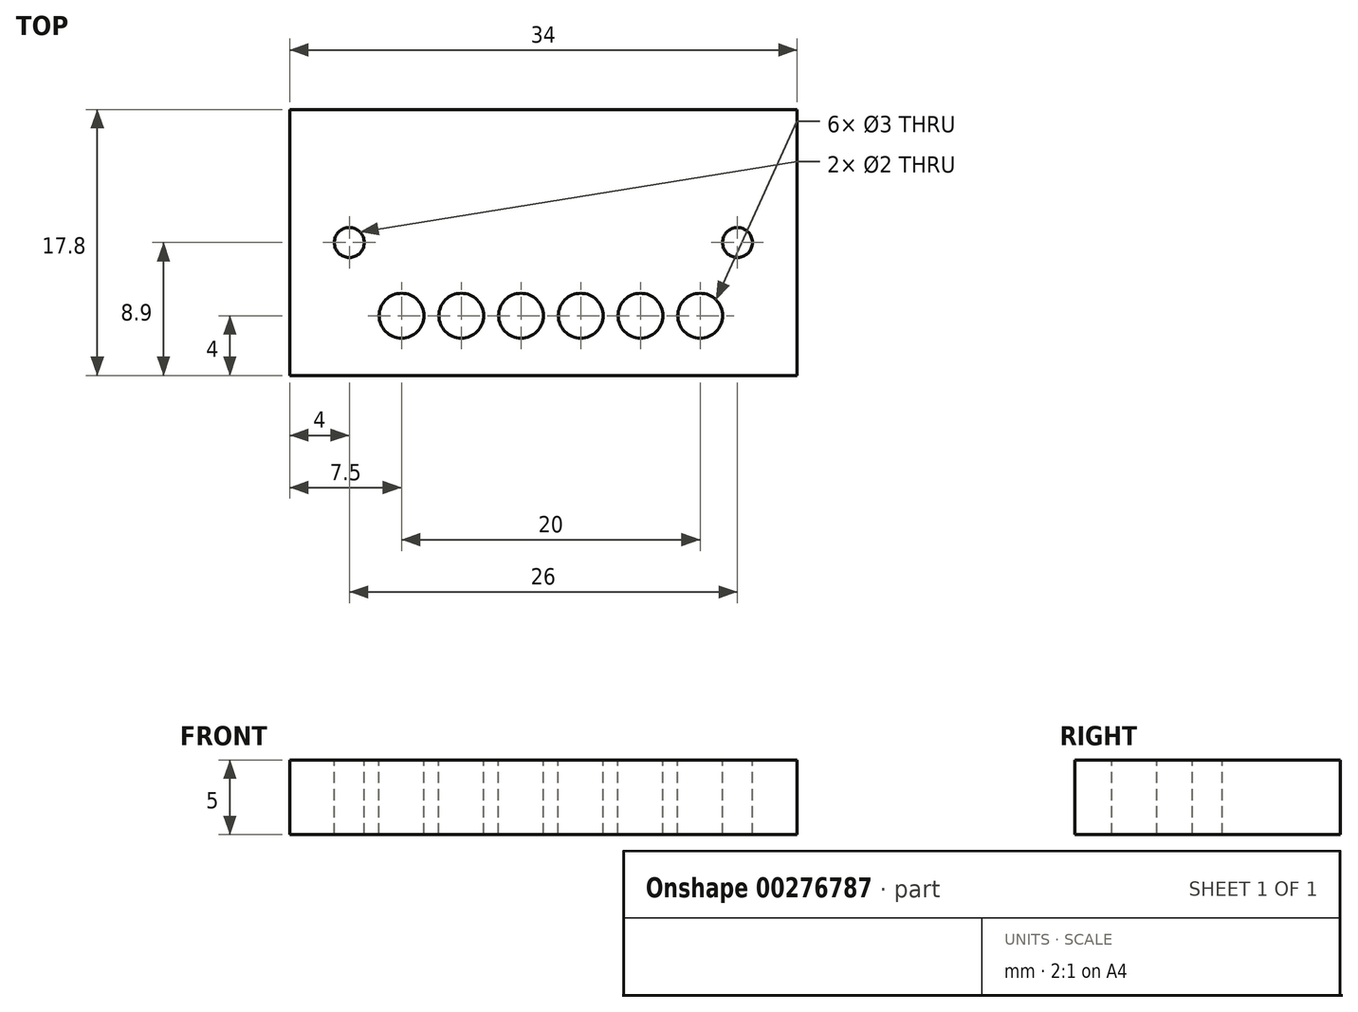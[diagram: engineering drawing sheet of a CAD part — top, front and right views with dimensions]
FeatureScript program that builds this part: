
annotation { "Feature Type Name" : "Feature", "Feature Type Description" : "" }
export const myFeature = defineFeature(function(context is Context, id is Id, definition is map)
    precondition{}
    {
        {
            var Q0;
            Q0=qCreatedBy(makeId("Top.planeOp"),FACE);
            var sketch = newSketch(context, id + "F0", { "sketchPlane" : qUnion([Q0])});
            skLineSegment(sketch, "E0.bottom", {"start": v(17, 8.9) * mm, "end": v(-17, 8.9) * mm});
            skLineSegment(sketch, "E0.top", {"start": v(17, -8.9) * mm, "end": v(-17, -8.9) * mm});
            skLineSegment(sketch, "E0.left", {"start": v(17, 8.9) * mm, "end": v(17, -8.9) * mm});
            skLineSegment(sketch, "E0.right", {"start": v(-17, 8.9) * mm, "end": v(-17, -8.9) * mm});
            skPoint(sketch, "E0.middle", {"position": v(0, 0) * mm});
            skSolve(sketch);
        }
        {
            var Q0;
            Q0=makeQuery(id+"F0.imprint","IMPRINT",FACE,{"disambiguationData":[TD([[makeQuery(id+"F0.imprint","IMPRINT",EDGE,{"derivedFrom":sQuery(id+"F0.wireOp",EDGE,"E0.bottom")}),1.0]])]});
            extrude(context, id + "F1", {"entities" : qUnion([Q0]), "oppositeDirection" : true, "depth" : 5 * mm});
        }
        {
            var Q0;
            Q0=makeQuery(id+"F1.opExtrude","CAP_FACE",FACE,{"disambiguationData":[OSD([sQuery(id+"F0.wireOp",EDGE,"E0.bottom"),sQuery(id+"F0.wireOp",EDGE,"E0.top"),sQuery(id+"F0.wireOp",EDGE,"E0.left"),sQuery(id+"F0.wireOp",EDGE,"E0.right")])],"isStart":true});
            var sketch = newSketch(context, id + "F2", { "sketchPlane" : qUnion([Q0])});
            skCircle(sketch, "E1", {"center": v(-13, 0) * mm, "radius": 1 * mm});
            skSolve(sketch);
        }
        {
            var Q0;
            Q0=sQuery(id+"F2.wireOp",VERTEX,"E1.center");
            var Q1;
            Q1=makeQuery(id+"F1.opExtrude","SWEPT_BODY",BODY,{"disambiguationData":[OSD([sQuery(id+"F0.wireOp",EDGE,"E0.bottom"),sQuery(id+"F0.wireOp",EDGE,"E0.top"),sQuery(id+"F0.wireOp",EDGE,"E0.left"),sQuery(id+"F0.wireOp",EDGE,"E0.right")])]});
            hole(context, id + "F3", {"style" : HoleStyle.SIMPLE, "endStyle" : HoleEndStyle.THROUGH, "holeDiameter" : 2 * mm, "tappedDepth" : 12.7 * mm, "tapClearance" : 3, "locations" : qUnion([Q0]), "scope" : qUnion([Q1])});
        }
        {
            var Q0;
            Q0=qCreatedBy(makeId("Top.planeOp"),FACE);
            var sketch = newSketch(context, id + "F4", { "sketchPlane" : qUnion([Q0])});
            skCircle(sketch, "E2", {"center": v(13, 0) * mm, "radius": 1 * mm});
            skSolve(sketch);
        }
        {
            var Q0;
            Q0=sQuery(id+"F4.wireOp",VERTEX,"E2.center");
            var Q1;
            Q1=makeQuery(id+"F1.opExtrude","SWEPT_BODY",BODY,{"disambiguationData":[OSD([sQuery(id+"F0.wireOp",EDGE,"E0.bottom"),sQuery(id+"F0.wireOp",EDGE,"E0.top"),sQuery(id+"F0.wireOp",EDGE,"E0.left"),sQuery(id+"F0.wireOp",EDGE,"E0.right")])]});
            hole(context, id + "F5", {"style" : HoleStyle.SIMPLE, "endStyle" : HoleEndStyle.THROUGH, "holeDiameter" : 2 * mm, "tappedDepth" : 12.7 * mm, "tapClearance" : 3, "locations" : qUnion([Q0]), "scope" : qUnion([Q1])});
        }
        {
            var Q0;
            Q0=makeQuery(id+"F1.opExtrude","CAP_FACE",FACE,{"disambiguationData":[OSD([sQuery(id+"F0.wireOp",EDGE,"E0.bottom"),sQuery(id+"F0.wireOp",EDGE,"E0.top"),sQuery(id+"F0.wireOp",EDGE,"E0.left"),sQuery(id+"F0.wireOp",EDGE,"E0.right")])],"isStart":true});
            var sketch = newSketch(context, id + "F6", { "sketchPlane" : qUnion([Q0])});
            skCircle(sketch, "E3", {"center": v(-9.5, -4.9) * mm, "radius": 1.5 * mm});
            skLineSegment(sketch, "E4", {"start": v(-9.5, -4.9) * mm, "end": v(-5.5, -4.9) * mm});
            skCircle(sketch, "E5", {"center": v(-5.5, -4.9) * mm, "radius": 1.5 * mm});
            skLineSegment(sketch, "E6", {"start": v(-9.5, -4.9) * mm, "end": v(-1.5, -4.9) * mm});
            skCircle(sketch, "E7", {"center": v(-1.5, -4.9) * mm, "radius": 1.5 * mm});
            skLineSegment(sketch, "E8", {"start": v(-9.5, -4.9) * mm, "end": v(2.5, -4.9) * mm});
            skCircle(sketch, "E9", {"center": v(2.5, -4.9) * mm, "radius": 1.5 * mm});
            skLineSegment(sketch, "E10", {"start": v(-9.5, -4.9) * mm, "end": v(6.5, -4.9) * mm});
            skCircle(sketch, "E11", {"center": v(6.5, -4.9) * mm, "radius": 1.5 * mm});
            skLineSegment(sketch, "E12", {"start": v(-9.5, -4.9) * mm, "end": v(10.5, -4.9) * mm});
            skCircle(sketch, "E13", {"center": v(10.5, -4.9) * mm, "radius": 1.5 * mm});
            skSolve(sketch);
        }
        {
            var Q0;
            Q0=sQuery(id+"F6.wireOp",VERTEX,"E3.center");
            var Q1;
            Q1=sQuery(id+"F6.wireOp",VERTEX,"E5.center");
            var Q2;
            Q2=sQuery(id+"F6.wireOp",VERTEX,"E7.center");
            var Q3;
            Q3=sQuery(id+"F6.wireOp",VERTEX,"E8.end");
            var Q4;
            Q4=sQuery(id+"F6.wireOp",VERTEX,"E10.end");
            var Q5;
            Q5=sQuery(id+"F6.wireOp",VERTEX,"E12.end");
            var Q6;
            Q6=makeQuery(id+"F1.opExtrude","SWEPT_BODY",BODY,{"disambiguationData":[OSD([sQuery(id+"F0.wireOp",EDGE,"E0.bottom"),sQuery(id+"F0.wireOp",EDGE,"E0.top"),sQuery(id+"F0.wireOp",EDGE,"E0.left"),sQuery(id+"F0.wireOp",EDGE,"E0.right")])]});
            hole(context, id + "F7", {"style" : HoleStyle.SIMPLE, "endStyle" : HoleEndStyle.THROUGH, "holeDiameter" : 3 * mm, "tappedDepth" : 12.7 * mm, "tapClearance" : 3, "locations" : qUnion([Q0, Q1, Q2, Q3, Q4, Q5]), "scope" : qUnion([Q6])});
        }
    });
